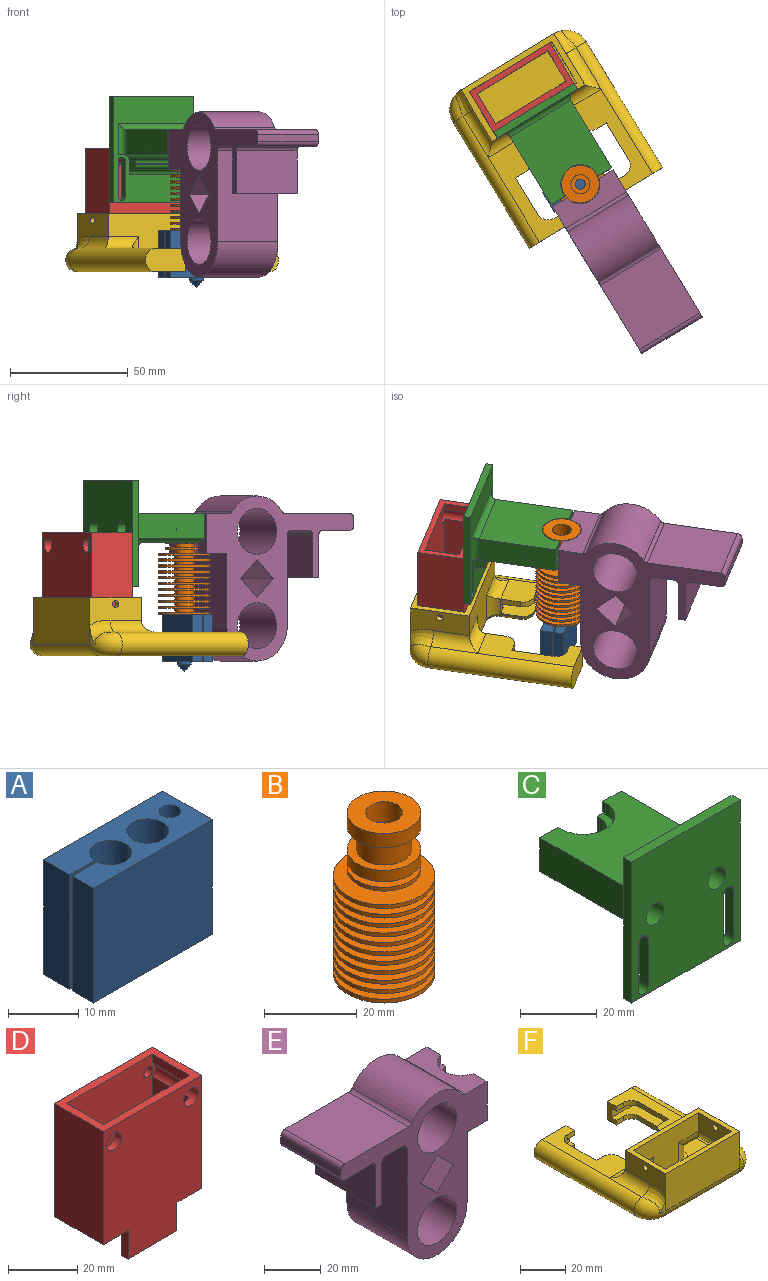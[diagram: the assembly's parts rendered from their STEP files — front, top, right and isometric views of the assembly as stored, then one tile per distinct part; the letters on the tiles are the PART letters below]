
ASSEMBLY  parts=6 mates=15
PART A: 15 faces, bbox 24x10x24.3 mm
  f0: plane 20x4.25mm, normal (-1,0,0), area 85mm2, adj f2,f3,f5,f14
  f1: cylinder r=3mm len=20mm, axis (0,0,-1), area 367mm2, adj f2,f3,f13,f14
  f2: plane 24x10mm, normal (0,0,1), area 173.4mm2, adj f0,f1,f4,f5,f6,f7,f8,f9
  f3: plane 24x10mm, normal (0,0,-1), area 172.4mm2, adj f0,f1,f4,f5,f6,f8,f9,f11
  f4: plane 20x5.25mm, normal (-1,0,0), area 105mm2, adj f2,f3,f9,f13
  f5: plane 24x20mm, normal (0,-1,0), area 480mm2, adj f0,f2,f3,f6
  f6: plane 20x10mm, normal (1,0,0), area 200mm2, adj f2,f3,f5,f9
  f7: cylinder r=3mm len=20mm, axis (0,0,-1), area 377mm2, adj f2,f12
  f8: cylinder r=1.55mm len=20mm, axis (0,0,-1), area 194.8mm2, adj f2,f3
  f9: plane 24x20mm, normal (0,1,0), area 480mm2, adj f2,f3,f4,f6
  f10: cone r=3.05mm half-angle=44.8deg, axis (0,0,1), area 41.5mm2, adj f11
  f11: cylinder r=3.05mm len=6.1mm, axis (0,0,-1), area 23.8mm2, adj f3,f10
  f12: plane 6x6mm, normal (0,0,1), area 28.3mm2, adj f7
  f13: plane 20x5.01mm, normal (0,-1,0), area 100.2mm2, adj f1,f2,f3,f4
  f14: plane 20x5.01mm, normal (0,1,0), area 100.2mm2, adj f0,f1,f2,f3
PART B: 60 faces, bbox 22x22x42.7 mm
  f0: cylinder r=4mm len=8mm, axis (0,0,1), area 163.4mm2, adj f1,f59
  f1: plane 16x16mm, normal (0,0,1), area 150.8mm2, adj f0,f2
  f2: cylinder r=8mm len=16mm, axis (0,0,1), area 186mm2, adj f1,f3
  f3: plane 16x16mm, normal (0,0,-1), area 88mm2, adj f2,f4
  f4: cylinder r=6mm len=12mm, axis (0,0,1), area 226.2mm2, adj f3,f5
  f5: plane 16x16mm, normal (0,0,1), area 88mm2, adj f4,f6
  f6: cylinder r=8mm len=16mm, axis (0,0,1), area 150.8mm2, adj f5,f7
  f7: plane 16x16mm, normal (0,0,-1), area 150.8mm2, adj f6,f8
  f8: cylinder r=4mm len=8mm, axis (0,0,1), area 37.7mm2, adj f7,f9
  f9: plane 16x16mm, normal (0,0,1), area 150.8mm2, adj f8,f10
  f10: cylinder r=8mm len=16mm, axis (0,0,1), area 50.3mm2, adj f9,f11
  f11: plane 16x16mm, normal (0,0,-1), area 150.8mm2, adj f10,f12
  f12: cylinder r=4mm len=8mm, axis (0,0,1), area 37.7mm2, adj f11,f13
  f13: plane 22x22mm, normal (0,0,1), area 329.9mm2, adj f12,f14
  f14: cylinder r=11mm len=22mm, axis (0,0,1), area 69.1mm2, adj f13,f15
  f15: plane 22x22mm, normal (0,0,-1), area 329.9mm2, adj f14,f16
  f16: cylinder r=4mm len=8mm, axis (0,0,1), area 37.7mm2, adj f15,f17
  f17: plane 22x22mm, normal (0,0,1), area 329.9mm2, adj f16,f18
  f18: cylinder r=11mm len=22mm, axis (0,0,1), area 69.1mm2, adj f17,f19
  f19: plane 22x22mm, normal (0,0,-1), area 329.9mm2, adj f18,f20
  f20: cylinder r=4mm len=8mm, axis (0,0,1), area 37.7mm2, adj f19,f21
  f21: plane 22x22mm, normal (0,0,1), area 329.9mm2, adj f20,f22
  f22: cylinder r=11mm len=22mm, axis (0,0,1), area 69.1mm2, adj f21,f23
  f23: plane 22x22mm, normal (0,0,-1), area 329.9mm2, adj f22,f24
  f24: cylinder r=4mm len=8mm, axis (0,0,1), area 37.7mm2, adj f23,f25
  f25: plane 22x22mm, normal (0,0,1), area 329.9mm2, adj f24,f26
  f26: cylinder r=11mm len=22mm, axis (0,0,1), area 69.1mm2, adj f25,f27
  f27: plane 22x22mm, normal (0,0,-1), area 329.9mm2, adj f26,f28
  f28: cylinder r=4mm len=8mm, axis (0,0,1), area 37.7mm2, adj f27,f29
  f29: plane 22x22mm, normal (0,0,1), area 329.9mm2, adj f28,f30
  f30: cylinder r=11mm len=22mm, axis (0,0,1), area 69.1mm2, adj f29,f31
  f31: plane 22x22mm, normal (0,0,-1), area 329.9mm2, adj f30,f32
  f32: cylinder r=4mm len=8mm, axis (0,0,1), area 37.7mm2, adj f31,f33
  f33: plane 22x22mm, normal (0,0,1), area 329.9mm2, adj f32,f34
  f34: cylinder r=11mm len=22mm, axis (0,0,1), area 69.1mm2, adj f33,f35
  f35: plane 22x22mm, normal (0,0,-1), area 329.9mm2, adj f34,f36
  f36: cylinder r=4mm len=8mm, axis (0,0,1), area 37.7mm2, adj f35,f37
  f37: plane 22x22mm, normal (0,0,1), area 329.9mm2, adj f36,f38
  f38: cylinder r=11mm len=22mm, axis (0,0,1), area 69.1mm2, adj f37,f39
  f39: plane 22x22mm, normal (0,0,-1), area 329.9mm2, adj f38,f40
  f40: cylinder r=4mm len=8mm, axis (0,0,1), area 37.7mm2, adj f39,f41
  f41: plane 22x22mm, normal (0,0,1), area 329.9mm2, adj f40,f42
  f42: cylinder r=11mm len=22mm, axis (0,0,1), area 69.1mm2, adj f41,f43
  f43: plane 22x22mm, normal (0,0,-1), area 329.9mm2, adj f42,f44
  f44: cylinder r=4mm len=8mm, axis (0,0,1), area 37.7mm2, adj f43,f45
  f45: plane 22x22mm, normal (0,0,1), area 329.9mm2, adj f44,f46
  f46: cylinder r=11mm len=22mm, axis (0,0,1), area 69.1mm2, adj f45,f47
  f47: plane 22x22mm, normal (0,0,-1), area 329.9mm2, adj f46,f48
  f48: cylinder r=4mm len=8mm, axis (0,0,1), area 37.7mm2, adj f47,f49
  f49: plane 22x22mm, normal (0,0,1), area 329.9mm2, adj f48,f50
  f50: cylinder r=11mm len=22mm, axis (0,0,1), area 69.1mm2, adj f49,f51
  f51: plane 22x22mm, normal (0,0,-1), area 329.9mm2, adj f50,f52
  f52: cylinder r=4mm len=8mm, axis (0,0,1), area 37.7mm2, adj f51,f53
  f53: plane 22x22mm, normal (0,0,1), area 329.9mm2, adj f52,f54
  f54: cylinder r=11mm len=22mm, axis (0,0,1), area 69.1mm2, adj f53,f55
  f55: plane 22x22mm, normal (0,0,-1), area 351.9mm2, adj f54,f56
  f56: cylinder r=3mm len=15.1mm, axis (0,0,1), area 284.6mm2, adj f55,f57
  f57: plane 6x6mm, normal (0,0,-1), area 14.4mm2, adj f56,f58
  f58: cylinder r=2.1mm len=21.1mm, axis (0,0,1), area 278.4mm2, adj f57,f59
  f59: plane 8x8mm, normal (0,0,1), area 36.4mm2, adj f0,f58
PART C: 51 faces, bbox 40x39x45 mm
  f0: plane 24x0.5mm, normal (0,0,-1), area 12mm2, adj f1,f2,f29,f42
  f1: plane 6x5.27mm, normal (-1,0,0), area 18.1mm2, adj f0,f3,f11,f29,f39,f41,f42
  f2: plane 6x5.27mm, normal (1,0,0), area 18.1mm2, adj f0,f4,f11,f29,f39,f41,f42
  f3: cylinder r=2.5mm len=36mm, axis (0,1,0), area 110.3mm2, adj f1,f11,f24,f40,f41,f50
  f4: cylinder r=2.5mm len=36mm, axis (0,1,0), area 110.3mm2, adj f2,f11,f25,f40,f41,f46
  f5: cylinder r=1.9mm len=14mm, axis (0,1,0), area 167.1mm2, adj f37,f46
  f6: cylinder r=1.9mm len=14mm, axis (0,1,0), area 167.1mm2, adj f35,f50
  f7: plane 33.5x30mm, normal (0,0,1), area 880.2mm2, adj f8,f9,f27,f34,f45,f46,f47,f50
  f8: plane 33.5x10.7mm, normal (1,0,0), area 358.4mm2, adj f7,f25,f26,f46
  f9: plane 33.5x10.7mm, normal (-1,0,0), area 358.4mm2, adj f7,f24,f28,f50
  f10: plane 45x40mm, normal (0,-1,0), area 1609.4mm2, adj f12,f13,f14,f15,f16,f17,f18,f19
  f11: plane 45x40mm, normal (0,1,0), area 1007.1mm2, adj f1,f2,f3,f4,f12,f13,f14,f15
  f12: plane 45x3mm, normal (1,0,0), area 135mm2, adj f10,f11,f13,f15
  f13: plane 40x3mm, normal (0,0,1), area 120mm2, adj f10,f11,f12,f14
  f14: plane 45x3mm, normal (-1,0,0), area 135mm2, adj f10,f11,f13,f15
  f15: plane 40x3mm, normal (0,0,-1), area 120mm2, adj f10,f11,f12,f14
  f16: cylinder r=1.75mm len=3.5mm, axis (0,-1,0), area 16.5mm2, adj f10,f11,f17,f18
  f17: plane 15x3mm, normal (-1,0,0), area 45mm2, adj f10,f11,f16,f19
  f18: plane 15x3mm, normal (1,0,0), area 45mm2, adj f10,f11,f16,f19
  f19: cylinder r=1.75mm len=3.5mm, axis (0,-1,0), area 16.5mm2, adj f10,f11,f17,f18
  f20: cylinder r=1.75mm len=3.5mm, axis (0,-1,0), area 16.5mm2, adj f10,f11,f22,f23
  f21: cylinder r=1.75mm len=3.5mm, axis (0,-1,0), area 16.5mm2, adj f10,f11,f22,f23
  f22: plane 15x3mm, normal (1,0,0), area 45mm2, adj f10,f11,f20,f21
  f23: plane 15x3mm, normal (-1,0,0), area 45mm2, adj f10,f11,f20,f21
  f24: plane 36x3mm, normal (0,0,-1), area 19.3mm2, adj f3,f9,f11,f28,f50
  f25: plane 36x3mm, normal (0,0,-1), area 19.3mm2, adj f4,f8,f11,f26,f46
  f26: cylinder r=2.5mm len=13.2mm, axis (0,0,-1), area 45.6mm2, adj f8,f11,f25,f27
  f27: cylinder r=2.5mm len=35mm, axis (1,0,0), area 124.9mm2, adj f7,f11,f26,f28
  f28: cylinder r=2.5mm len=13.2mm, axis (0,0,1), area 45.6mm2, adj f9,f11,f24,f27
  f29: cylinder r=2.5mm len=24mm, axis (-1,0,0), area 94.2mm2, adj f0,f1,f2,f11
  f30: plane 16.6x9.3mm, normal (0,0,1), area 52mm2, adj f31,f34,f44,f45,f46,f47,f48,f50
  f31: cylinder r=6.2mm len=12.4mm, axis (0,0,1), area 113mm2, adj f30,f32,f44,f48
  f32: plane 16.6x9.3mm, normal (0,0,-1), area 52mm2, adj f31,f33,f43,f44,f46,f48,f49,f50
  f33: cylinder r=8.3mm len=16.6mm, axis (0,0,1), area 70.4mm2, adj f32,f40,f43,f49
  f34: cylinder r=8.3mm len=16.6mm, axis (0,0,1), area 96.5mm2, adj f7,f30,f45,f47
  f35: plane 6.5x6.5mm, normal (0,-1,0), area 21.8mm2, adj f6,f36
  f36: cylinder r=3.25mm len=25mm, axis (0,-1,0), area 510.5mm2, adj f10,f35
  f37: plane 6.5x6.5mm, normal (0,-1,0), area 21.8mm2, adj f5,f38
  f38: cylinder r=3.25mm len=25mm, axis (0,-1,0), area 510.5mm2, adj f10,f37
  f39: plane 24x0.5mm, normal (0,1,0), area 12mm2, adj f1,f2,f41,f42
  f40: plane 29x24.42mm, normal (0,0,-1), area 583.3mm2, adj f3,f4,f33,f41,f43,f46,f49,f50
  f41: cylinder r=2mm len=24.42mm, axis (1,0,0), area 75.8mm2, adj f1,f2,f3,f4,f39,f40
  f42: cylinder r=2mm len=24mm, axis (1,0,0), area 75.4mm2, adj f0,f1,f2,f39
  f43: plane 2.7x1mm, normal (-1,0,0), area 2.7mm2, adj f32,f33,f40,f46
  f44: plane 5.8x1mm, normal (-1,0,0), area 5.8mm2, adj f30,f31,f32,f46
  f45: plane 3.7x1mm, normal (-1,0,0), area 3.7mm2, adj f7,f30,f34,f46
  f46: plane 12.2x8.8mm, normal (0,1,0), area 79.4mm2, adj f4,f5,f7,f8,f25,f30,f32,f40
  f47: plane 3.7x1mm, normal (1,0,0), area 3.7mm2, adj f7,f30,f34,f50
  f48: plane 5.8x1mm, normal (1,0,0), area 5.8mm2, adj f30,f31,f32,f50
  f49: plane 2.7x1mm, normal (1,0,0), area 2.7mm2, adj f32,f33,f40,f50
  f50: plane 12.2x8.8mm, normal (0,1,0), area 79.4mm2, adj f3,f6,f7,f9,f24,f30,f32,f40
PART D: 23 faces, bbox 40x20x50 mm
  f0: plane 40x20mm, normal (1,0,0), area 800mm2, adj f4,f10,f11,f20
  f1: plane 40x20mm, normal (-1,0,0), area 800mm2, adj f4,f10,f11,f18
  f2: plane 20x2.5mm, normal (0,0,-1), area 50mm2, adj f4,f6,f17,f21
  f3: plane 20x2.5mm, normal (0,0,-1), area 50mm2, adj f7,f11,f19,f22
  f4: plane 50x40mm, normal (0,-1,0), area 1743.5mm2, adj f0,f1,f2,f10,f13,f14,f17,f18
  f5: plane 32.06x15mm, normal (-1,0,0), area 480.9mm2, adj f6,f7,f13,f20
  f6: plane 50x35mm, normal (0,1,0), area 1552mm2, adj f2,f5,f8,f9,f10,f12,f13,f14
  f7: plane 50x37.5mm, normal (0,-1,0), area 1589.3mm2, adj f3,f5,f8,f9,f10,f12,f13,f14
  f8: plane 15x3.06mm, normal (-1,0,0), area 45.9mm2, adj f6,f7,f10,f13
  f9: plane 15x3.06mm, normal (1,0,0), area 45.9mm2, adj f6,f7,f10,f14
  f10: plane 40x20mm, normal (0,0,1), area 275mm2, adj f0,f1,f4,f6,f7,f8,f9,f11
  f11: plane 50x40mm, normal (0,1,0), area 1780.8mm2, adj f0,f1,f3,f10,f15,f16,f18,f19
  f12: plane 32.06x15mm, normal (1,0,0), area 480.9mm2, adj f6,f7,f14,f18
  f13: cylinder r=3mm len=17.5mm, axis (0,-1,0), area 132.4mm2, adj f4,f5,f6,f7,f8
  f14: cylinder r=3mm len=17.5mm, axis (0,-1,0), area 132.4mm2, adj f4,f6,f7,f9,f12
  f15: cylinder r=1.75mm len=3.5mm, axis (0,-1,0), area 27.5mm2, adj f7,f11
  f16: cylinder r=1.75mm len=3.5mm, axis (0,-1,0), area 27.5mm2, adj f7,f11
  f17: plane 10x2.5mm, normal (-1,0,0), area 25mm2, adj f2,f4,f6,f18
  f18: plane 20x10mm, normal (0,0,-1), area 87.5mm2, adj f1,f4,f6,f7,f11,f12,f17,f19
  f19: plane 10x2.5mm, normal (-1,0,0), area 25mm2, adj f3,f7,f11,f18
  f20: plane 20x10mm, normal (0,0,-1), area 87.5mm2, adj f0,f4,f5,f6,f7,f11,f21,f22
  f21: plane 10x2.5mm, normal (1,0,0), area 25mm2, adj f2,f4,f6,f20
  f22: plane 10x2.5mm, normal (1,0,0), area 25mm2, adj f3,f7,f11,f20
PART E: 35 faces, bbox 73x30x70 mm
  f0: plane 30x13.4mm, normal (0,0,-1), area 402mm2, adj f12,f13,f24,f29
  f1: plane 30x10.89mm, normal (0,0,1), area 251.4mm2, adj f2,f12,f13,f15,f16,f26
  f2: plane 16.7x9.13mm, normal (1,0,0), area 128.7mm2, adj f1,f12,f14,f16,f17,f18,f19,f20
  f3: plane 30.78x30mm, normal (1,0,0), area 923.5mm2, adj f10,f12,f13,f14
  f4: cylinder r=15mm len=30mm, axis (0,1,0), area 881.1mm2, adj f12,f13,f26,f27
  f5: plane 31.89x30mm, normal (0,0,1), area 956.7mm2, adj f12,f13,f27,f28
  f6: plane 30x3mm, normal (-1,0,0), area 90mm2, adj f12,f13,f28,f29
  f7: plane 30x8.6mm, normal (0,0,-1), area 258mm2, adj f12,f13,f25,f30
  f8: plane 38.48x30mm, normal (-1,0,0), area 1154.5mm2, adj f10,f12,f13,f30
  f9: cylinder r=9.75mm len=30mm, axis (0,1,0), area 1837.8mm2, adj f12,f13
  f10: cylinder r=15mm len=30mm, axis (0,1,0), area 1413.7mm2, adj f3,f8,f12,f13
  f11: cylinder r=9.75mm len=30mm, axis (0,1,0), area 1837.8mm2, adj f12,f13
  f12: plane 73x70mm, normal (0,-1,0), area 1646.2mm2, adj f0,f1,f2,f3,f4,f5,f6,f7
  f13: plane 73x70mm, normal (0,1,0), area 1646.2mm2, adj f0,f1,f3,f4,f5,f6,f7,f8
  f14: plane 30x10mm, normal (0,0,-1), area 224.7mm2, adj f2,f3,f12,f13,f15,f20
  f15: plane 16.7x9.13mm, normal (1,0,0), area 128.7mm2, adj f1,f13,f14,f16,f17,f18,f19,f20
  f16: cylinder r=8.3mm len=16.11mm, axis (0,0,1), area 81.5mm2, adj f1,f2,f15,f17
  f17: plane 16.11x6.3mm, normal (0,0,1), area 39.3mm2, adj f2,f15,f16,f18
  f18: cylinder r=6.2mm len=11.74mm, axis (0,0,1), area 89.3mm2, adj f2,f15,f17,f19
  f19: plane 16.11x6.3mm, normal (0,0,-1), area 39.3mm2, adj f2,f15,f18,f20
  f20: cylinder r=8.3mm len=16.11mm, axis (0,0,1), area 158.7mm2, adj f2,f14,f15,f19
  f21: plane 30x18mm, normal (-1,0,0), area 540mm2, adj f12,f13,f22,f24
  f22: plane 30x3mm, normal (0,0,-1), area 90mm2, adj f12,f13,f21,f23
  f23: plane 30x18mm, normal (1,0,0), area 540mm2, adj f12,f13,f22,f25
  f24: cylinder r=2mm len=30mm, axis (0,1,0), area 94.2mm2, adj f0,f12,f13,f21
  f25: cylinder r=2mm len=30mm, axis (0,-1,0), area 94.2mm2, adj f7,f12,f13,f23
  f26: cylinder r=2mm len=30mm, axis (0,1,0), area 58.7mm2, adj f1,f4,f12,f13
  f27: cylinder r=2mm len=30mm, axis (0,1,0), area 58.7mm2, adj f4,f5,f12,f13
  f28: cylinder r=2mm len=30mm, axis (0,1,0), area 94.2mm2, adj f5,f6,f12,f13
  f29: cylinder r=2mm len=30mm, axis (0,-1,0), area 94.2mm2, adj f0,f6,f12,f13
  f30: cylinder r=2mm len=30mm, axis (0,1,0), area 94.2mm2, adj f7,f8,f12,f13
  f31: plane 30x8.13mm, normal (-0.71,0,-0.71), area 345mm2, adj f12,f13,f32,f34
  f32: plane 30x8.13mm, normal (0.71,0,-0.71), area 345mm2, adj f12,f13,f31,f33
  f33: plane 30x8.13mm, normal (0.71,0,0.71), area 345mm2, adj f12,f13,f32,f34
  f34: plane 30x8.13mm, normal (-0.71,0,0.71), area 345mm2, adj f12,f13,f31,f33
PART F: 97 faces, bbox 68.8x77.8x26.2 mm
  f0: plane 46x25.5mm, normal (0,0,1), area 332.5mm2, adj f21,f22,f23,f25,f46,f47,f48,f50
  f1: plane 10x5.5mm, normal (1,0,0), area 40mm2, adj f14,f15,f18,f24,f26,f44,f49,f51
  f2: plane 10x5.5mm, normal (-1,0,0), area 40mm2, adj f7,f8,f20,f24,f27,f45,f49,f52
  f3: plane 20x2.5mm, normal (1,0,0), area 45.9mm2, adj f13,f24,f49,f78,f79
  f4: plane 18x2.5mm, normal (1,0,0), area 45mm2, adj f12,f18,f44,f73
  f5: plane 4.5x2.5mm, normal (0,1,0), area 11.2mm2, adj f9,f20,f45,f72
  f6: plane 4.5x0.5mm, normal (0,1,0), area 2.3mm2, adj f10,f49,f76,f87
  f7: plane 4.5x2.5mm, normal (0,-1,0), area 11.3mm2, adj f2,f24,f49,f77
  f8: plane 4.5x2.5mm, normal (0,-1,0), area 11.3mm2, adj f2,f20,f45,f71
  f9: plane 18x2.5mm, normal (-1,0,0), area 45mm2, adj f5,f20,f45,f71
  f10: plane 20x2.5mm, normal (-1,0,0), area 45.9mm2, adj f6,f24,f49,f77,f87
  f11: plane 8.5x0.5mm, normal (-1,0,0), area 4.3mm2, adj f40,f49,f76,f85
  f12: plane 4.5x2.5mm, normal (0,1,0), area 11.3mm2, adj f4,f18,f44,f74
  f13: plane 4.5x0.5mm, normal (0,1,0), area 2.3mm2, adj f3,f49,f75,f79
  f14: plane 4.5x2.5mm, normal (0,-1,0), area 11.3mm2, adj f1,f24,f49,f78
  f15: plane 4.5x2.5mm, normal (0,-1,0), area 11.3mm2, adj f1,f18,f44,f73
  f16: plane 8.5x0.5mm, normal (1,0,0), area 4.3mm2, adj f41,f49,f75,f81
  f17: plane 8.5x2.5mm, normal (1,0,0), area 21.2mm2, adj f18,f41,f44,f74
  f18: plane 42x15mm, normal (0,0,1), area 411.5mm2, adj f1,f4,f12,f15,f17,f26,f29,f33
  f19: plane 8.5x2.5mm, normal (-1,0,0), area 21.2mm2, adj f20,f40,f45,f72
  f20: plane 42x15mm, normal (0,0,1), area 411.5mm2, adj f2,f5,f8,f9,f19,f27,f28,f35
  f21: plane 25.5x12.14mm, normal (-1,0,0), area 252.9mm2, adj f0,f23,f25,f38,f39,f70
  f22: plane 25.5x12.14mm, normal (1,0,0), area 252.9mm2, adj f0,f23,f25,f36,f37,f69
  f23: plane 46x23mm, normal (0,1,0), area 668mm2, adj f0,f21,f22,f28,f29,f40,f41,f83
  f24: plane 67.5x56mm, normal (0,0,-1), area 1974.2mm2, adj f1,f2,f3,f7,f10,f14,f26,f27
  f25: plane 46x20mm, normal (0,-1,0), area 920mm2, adj f0,f21,f22,f30,f31,f96
  f26: plane 20x10mm, normal (0,1,0), area 189.3mm2, adj f1,f18,f24,f33
  f27: plane 20x10mm, normal (0,1,0), area 189.3mm2, adj f2,f20,f24,f35
  f28: cylinder r=5mm len=20mm, axis (1,0,0), area 117.8mm2, adj f20,f23,f36,f40
  f29: cylinder r=5mm len=20mm, axis (1,0,0), area 117.8mm2, adj f18,f23,f38,f41
  f30: cylinder r=10mm len=7.86mm, axis (0,0,-1), area 13.4mm2, adj f25,f34,f37
  f31: cylinder r=10mm len=7.86mm, axis (0,0,1), area 13.4mm2, adj f25,f32,f39
  f32: torus R=5mm, axis (0,0,-1), area 170.8mm2, adj f24,f31,f33,f39,f96
  f33: cylinder r=5mm len=62.5mm, axis (0,-1,0), area 981.7mm2, adj f18,f24,f26,f32,f38
  f34: torus R=5mm, axis (0,0,-1), area 170.8mm2, adj f24,f30,f35,f37,f96
  f35: cylinder r=5mm len=62.5mm, axis (0,1,0), area 981.7mm2, adj f20,f24,f27,f34,f36
  f36: cylinder r=5mm len=20.5mm, axis (0,1,0), area 141.4mm2, adj f22,f28,f35,f37
  f37: bspline ~15.81x12.08mm, area 80.4mm2, adj f22,f30,f34,f36
  f38: cylinder r=5mm len=20.5mm, axis (0,-1,0), area 141.4mm2, adj f21,f29,f33,f39
  f39: bspline ~15.81x12.08mm, area 80.4mm2, adj f21,f31,f32,f38
  f40: cylinder r=5mm len=13mm, axis (0,0,1), area 77.1mm2, adj f11,f19,f23,f28,f43,f84
  f41: cylinder r=5mm len=13mm, axis (0,0,-1), area 77.1mm2, adj f16,f17,f23,f29,f42,f82
  f42: plane 5x4.5mm, normal (0,1,0), area 13.4mm2, adj f41,f44,f49,f68,f93
  f43: plane 5x4.5mm, normal (0,1,0), area 13.4mm2, adj f40,f45,f49,f67,f95
  f44: plane 39.5x15mm, normal (0,0,-1), area 374mm2, adj f1,f4,f12,f15,f17,f42,f51,f54
  f45: plane 39.5x15mm, normal (0,0,-1), area 374mm2, adj f2,f5,f8,f9,f19,f43,f52,f53
  f46: plane 20.5x10.84mm, normal (1,0,0), area 199.4mm2, adj f0,f48,f50,f65,f66,f70
  f47: plane 20.5x10.84mm, normal (-1,0,0), area 199.4mm2, adj f0,f48,f50,f63,f64,f69
  f48: plane 41x20.5mm, normal (0,-1,0), area 578mm2, adj f0,f46,f47,f53,f54,f67,f68,f94
  f49: plane 65.5x57mm, normal (0,0,1), area 1962.8mm2, adj f1,f2,f3,f6,f7,f10,f11,f13
  f50: plane 47.2x21.7mm, normal (0,1,0), area 867.1mm2, adj f0,f46,f47,f57,f58,f64,f66,f90
  f51: plane 17.5x5mm, normal (0,-1,0), area 85.3mm2, adj f1,f44,f49,f56,f60,f88
  f52: plane 17.5x5mm, normal (0,-1,0), area 85.3mm2, adj f2,f45,f49,f55,f62,f92
  f53: cylinder r=7.5mm len=20mm, axis (1,0,0), area 147.3mm2, adj f45,f48,f63,f67
  f54: cylinder r=7.5mm len=20mm, axis (1,0,0), area 147.3mm2, adj f44,f48,f65,f68
  f55: plane 60x0.5mm, normal (-1,0,0), area 30mm2, adj f52,f57,f62,f92
  f56: plane 60x0.5mm, normal (1,0,0), area 30mm2, adj f51,f58,f60,f88
  f57: cylinder r=7.5mm len=7.5mm, axis (0,0,-1), area 9.3mm2, adj f50,f55,f61,f64,f91
  f58: cylinder r=7.5mm len=7.5mm, axis (0,0,1), area 9.3mm2, adj f50,f56,f59,f66,f89
  f59: torus R=5mm, axis (0,0,-1), area 27.7mm2, adj f58,f60,f66
  f60: cylinder r=2.5mm len=60mm, axis (0,-1,0), area 235.6mm2, adj f44,f51,f56,f59,f65
  f61: torus R=5mm, axis (0,0,-1), area 27.7mm2, adj f57,f62,f64
  f62: cylinder r=2.5mm len=60mm, axis (0,1,0), area 235.6mm2, adj f45,f52,f55,f61,f63
  f63: cylinder r=7.5mm len=20.5mm, axis (0,1,0), area 197.3mm2, adj f47,f53,f62,f64
  f64: bspline ~15.81x12.08mm, area 86.5mm2, adj f47,f50,f57,f61,f63
  f65: cylinder r=7.5mm len=20.5mm, axis (0,-1,0), area 197.3mm2, adj f46,f54,f60,f66
  f66: bspline ~15.81x12.08mm, area 86.5mm2, adj f46,f50,f58,f59,f65
  f67: cylinder r=7.5mm len=10.5mm, axis (0,0,1), area 67.5mm2, adj f43,f48,f53,f95
  f68: cylinder r=7.5mm len=10.5mm, axis (0,0,-1), area 67.5mm2, adj f42,f48,f54,f93
  f69: cylinder r=1.5mm len=3mm, axis (-1,0,0), area 23.6mm2, adj f22,f47
  f70: cylinder r=1.5mm len=3mm, axis (-1,0,0), area 23.6mm2, adj f21,f46
  f71: cylinder r=5mm len=5mm, axis (0,0,1), area 19.6mm2, adj f8,f9,f20,f45
  f72: cylinder r=5mm len=5mm, axis (0,0,-1), area 19.6mm2, adj f5,f19,f20,f45
  f73: cylinder r=5mm len=5mm, axis (0,0,-1), area 19.6mm2, adj f4,f15,f18,f44
  f74: cylinder r=5mm len=5mm, axis (0,0,1), area 19.6mm2, adj f12,f17,f18,f44
  f75: cylinder r=5mm len=5mm, axis (0,0,1), area 3.9mm2, adj f13,f16,f49,f80
  f76: cylinder r=5mm len=5mm, axis (0,0,-1), area 3.9mm2, adj f6,f11,f49,f86
  f77: cylinder r=5mm len=5mm, axis (0,0,1), area 19.6mm2, adj f7,f10,f24,f49
  f78: cylinder r=5mm len=5mm, axis (0,0,-1), area 19.6mm2, adj f3,f14,f24,f49
  f79: cylinder r=2mm len=4.5mm, axis (1,0,0), area 14.1mm2, adj f3,f13,f24,f80
  f80: torus R=3mm, axis (0,0,-1), area 21.1mm2, adj f24,f75,f79,f81
  f81: cylinder r=2mm len=8.5mm, axis (0,-1,0), area 26.7mm2, adj f16,f24,f80,f82
  f82: torus R=7mm, axis (0,0,-1), area 28.3mm2, adj f24,f41,f81,f83
  f83: cylinder r=2mm len=16mm, axis (1,0,0), area 50.3mm2, adj f23,f24,f82,f84
  f84: torus R=7mm, axis (0,0,-1), area 28.3mm2, adj f24,f40,f83,f85
  f85: cylinder r=2mm len=8.5mm, axis (0,1,0), area 26.7mm2, adj f11,f24,f84,f86
  f86: torus R=3mm, axis (0,0,-1), area 21.1mm2, adj f24,f76,f85,f87
  f87: cylinder r=2mm len=4.5mm, axis (1,0,0), area 14.1mm2, adj f6,f10,f24,f86
  f88: cylinder r=2mm len=60mm, axis (0,-1,0), area 188.5mm2, adj f49,f51,f56,f89
  f89: torus R=5.5mm, axis (0,0,-1), area 33.4mm2, adj f49,f58,f88,f90
  f90: cylinder r=2mm len=46mm, axis (1,0,0), area 144.5mm2, adj f49,f50,f89,f91
  f91: torus R=5.5mm, axis (0,0,-1), area 33.4mm2, adj f49,f57,f90,f92
  f92: cylinder r=2mm len=60mm, axis (0,1,0), area 188.5mm2, adj f49,f52,f55,f91
  f93: torus R=9.5mm, axis (0,0,-1), area 40.6mm2, adj f42,f49,f68,f94
  f94: cylinder r=2mm len=16mm, axis (-1,0,0), area 50.3mm2, adj f48,f49,f93,f95
  f95: torus R=9.5mm, axis (0,0,-1), area 40.6mm2, adj f43,f49,f67,f94
  f96: cylinder r=5mm len=46mm, axis (-1,0,0), area 361.3mm2, adj f24,f25,f32,f34
PLACE A rot(axis=(0,0,1),31.2deg) t=(-13.25,-8.04,-52.7)mm
PLACE B at identity
PLACE C rot(axis=(0,0,-1),148.8deg) t=(0,0,-8.35)mm
PLACE D rot(axis=(0,0,-1),148.8deg) t=(-19.71,32.49,-32.85)mm
PLACE E rot(axis=(0,0,1),121.2deg) t=(14,-23.09,-27.48)mm
PLACE F rot(axis=(0,0,-1),148.8deg) t=(-17.72,30.19,-47.85)mm
MATE cylindrical D.f13 <-> C.f19  axis (-0.52,0.86,0) through (-33.82,25.39,-13.35)mm
MATE planar E.f1 <-> B.f0  axis (0,0,1) through (6.69,-11.02,0)mm
MATE cylindrical C.f31 <-> B.f0  axis (0,0,1) through (0,0,-3.7)mm
MATE planar D.f11 <-> C.f10  axis (0.52,-0.86,0) through (-19.71,32.49,-30.81)mm
MATE cylindrical A.f7 <-> B.f0  axis (0,0,-1) through (0,0,-52.7)mm
MATE planar A.f2 <-> B.f0  axis (0,0,1) through (-11.24,-6.53,-42.7)mm
MATE parallel A.f6 <-> E.f12  axis (0.86,0.52,0) through (7.01,4.84,-52.7)mm
MATE planar F.f49 <-> D.f2  axis (0,0,1) through (-16.23,27.72,-57.85)mm
MATE planar D.f7 <-> D.f7  axis (-0.52,0.86,0) through (-21,34.63,-31.09)mm
MATE planar D.f0 <-> F.f47  axis (-0.86,-0.52,0) through (-41.99,30.67,-27.85)mm
MATE planar D.f1 <-> C.f14  axis (0.86,0.52,0) through (-7.79,51.41,-27.85)mm
MATE planar D.f4 <-> F.f50  axis (-0.52,0.86,0) through (-30.08,49.59,-31.19)mm
MATE parallel E.f15 <-> C.f46  axis (-0.52,0.86,0) through (-5.85,-5.89,-3.7)mm
MATE planar E.f1 <-> C.f7  axis (0,0,1) through (4.3,-7.09,0)mm
MATE cylindrical E.f16 <-> B.f0  axis (0,0,1) through (0,0,-6.6)mm
